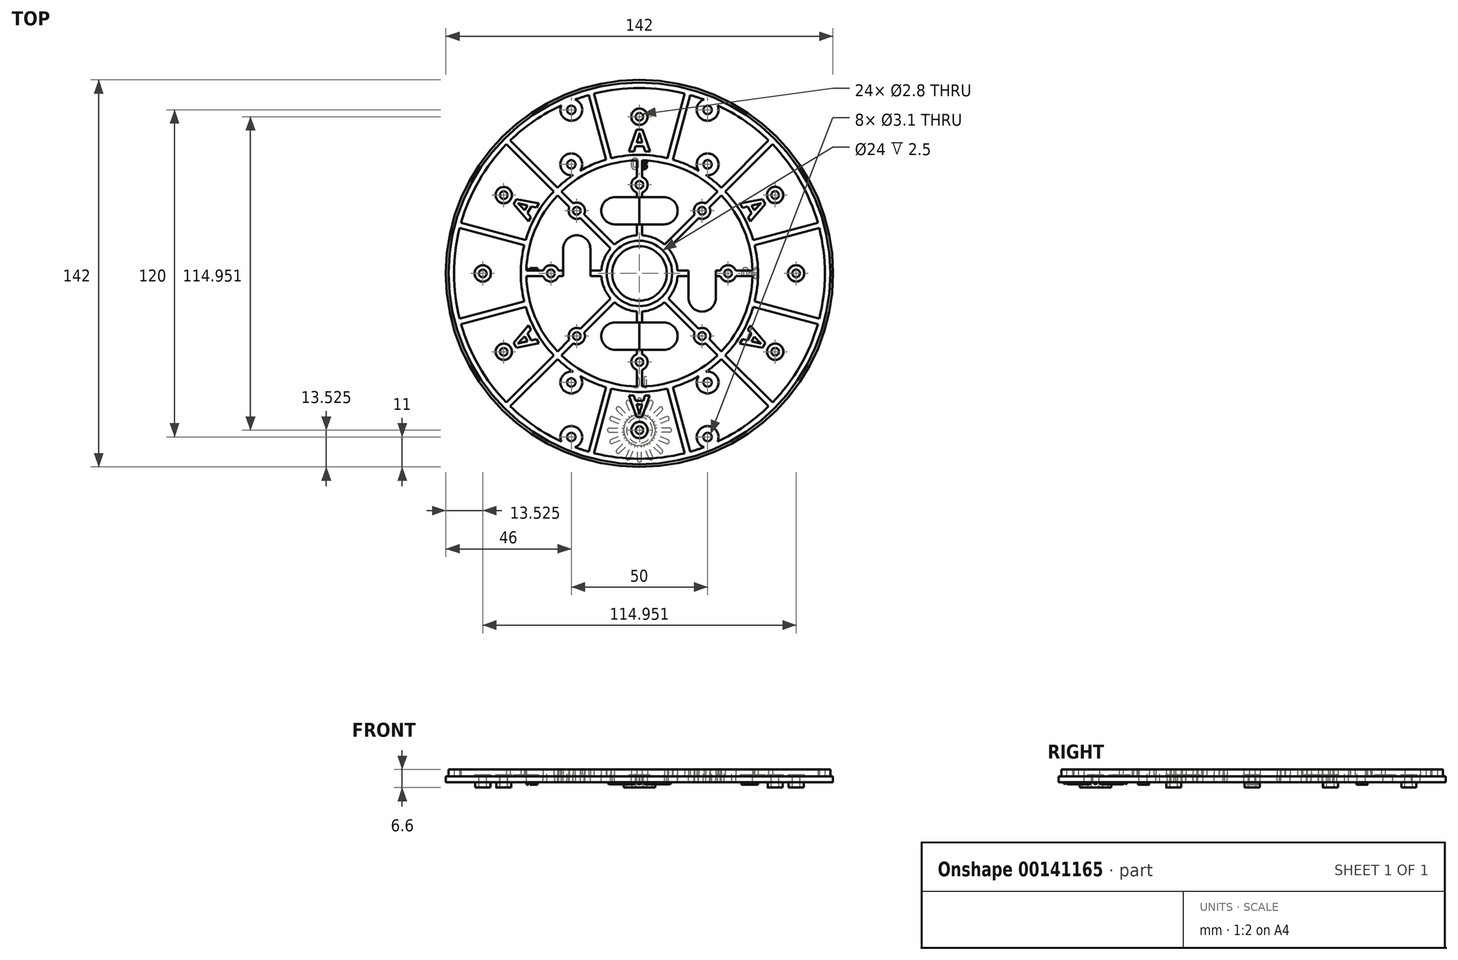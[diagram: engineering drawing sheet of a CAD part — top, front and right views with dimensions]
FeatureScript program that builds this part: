
annotation { "Feature Type Name" : "Feature", "Feature Type Description" : "" }
export const myFeature = defineFeature(function(context is Context, id is Id, definition is map)
    precondition{}
    {
        {
            var Q0;
            Q0=qCreatedBy(makeId("Top.planeOp"),FACE);
            var sketch = newSketch(context, id + "F0", { "sketchPlane" : qUnion([Q0])});
            skCircle(sketch, "E0", {"center": v(0, 0) * mm, "radius": 71 * mm});
            skCircle(sketch, "E1", {"center": v(0, 0) * mm, "radius": 10 * mm});
            skLineSegment(sketch, "E2.top", {"start": v(9, 18) * mm, "end": v(-9, 18) * mm});
            skLineSegment(sketch, "E3.top", {"start": v(-9, 28) * mm, "end": v(9, 28) * mm});
            skCircle(sketch, "E4", {"center": v(0, 0) * mm, "radius": 32.5 * mm, "construction": true});
            skArc(sketch, "E5", {"start": v(-9, 28) * mm, "mid": v(-14, 23) * mm, "end": v(-9, 18) * mm});
            skArc(sketch, "E6.MirrorC", {"start": v(9, 28) * mm, "mid": v(14, 23) * mm, "end": v(9, 18) * mm});
            skLineSegment(sketch, "E7.1.0", {"start": v(-18, 9) * mm, "end": v(-18, -9) * mm});
            skLineSegment(sketch, "E7.1.1", {"start": v(-28, -9) * mm, "end": v(-28, 9) * mm});
            skArc(sketch, "E7.1.2", {"start": v(-28, 9) * mm, "mid": v(-23, 14) * mm, "end": v(-18, 9) * mm});
            skArc(sketch, "E7.1.3", {"start": v(-28, -9) * mm, "mid": v(-23, -14) * mm, "end": v(-18, -9) * mm});
            skLineSegment(sketch, "E7.2.0", {"start": v(-9, -18) * mm, "end": v(9, -18) * mm});
            skLineSegment(sketch, "E7.2.1", {"start": v(9, -28) * mm, "end": v(-9, -28) * mm});
            skArc(sketch, "E7.2.2", {"start": v(-9, -28) * mm, "mid": v(-14, -23) * mm, "end": v(-9, -18) * mm});
            skArc(sketch, "E7.2.3", {"start": v(9, -28) * mm, "mid": v(14, -23) * mm, "end": v(9, -18) * mm});
            skLineSegment(sketch, "E7.3.0", {"start": v(18, -9) * mm, "end": v(18, 9) * mm});
            skLineSegment(sketch, "E7.3.1", {"start": v(28, 9) * mm, "end": v(28, -9) * mm});
            skArc(sketch, "E7.3.2", {"start": v(28, -9) * mm, "mid": v(23, -14) * mm, "end": v(18, -9) * mm});
            skArc(sketch, "E7.3.3", {"start": v(28, 9) * mm, "mid": v(23, 14) * mm, "end": v(18, 9) * mm});
            skCircle(sketch, "E8", {"center": v(0, 0) * mm, "radius": 42.5 * mm, "construction": true});
            skPoint(sketch, "E9", {"position": v(0, 32.5) * mm});
            skCircle(sketch, "E10", {"center": v(0, 0) * mm, "radius": 57.5 * mm, "construction": true});
            skLineSegment(sketch, "E11", {"start": v(-42.5, 0) * mm, "end": v(42.5, 0) * mm, "construction": true});
            skLineSegment(sketch, "E12", {"start": v(0, 42.5) * mm, "end": v(0, -42.5) * mm});
            skLineSegment(sketch, "E13", {"start": v(-7.07, 7.07) * mm, "end": v(-50.2, 50.2) * mm, "construction": true});
            skArc(sketch, "E14.0", {"start": v(-48.79, 47.37) * mm, "mid": v(-58.89, 34) * mm, "end": v(-65.42, 18.56) * mm});
            skCircle(sketch, "E15.0", {"center": v(0, 0) * mm, "radius": 70 * mm});
            skArc(sketch, "E16.0", {"start": v(-31.46, 30.04) * mm, "mid": v(-37.67, 21.75) * mm, "end": v(-41.75, 12.22) * mm});
            skArc(sketch, "E17.0", {"start": v(-41.49, -1) * mm, "mid": v(-38.34, -15.88) * mm, "end": v(-30.04, -28.63) * mm});
            skCircle(sketch, "E18.0", {"center": v(0, 0) * mm, "radius": 12 * mm});
            skArc(sketch, "E19.0", {"start": v(-10.58, 9.17) * mm, "mid": v(-12.93, 5.36) * mm, "end": v(-13.96, 1) * mm});
            skLineSegment(sketch, "E20.0", {"start": v(1, 42.5) * mm, "end": v(1, 42.49) * mm});
            skLineSegment(sketch, "E21.0", {"start": v(-1, 42.5) * mm, "end": v(-1, 42.49) * mm});
            skLineSegment(sketch, "E22.0", {"start": v(-42.5, -1) * mm, "end": v(-42.49, -1) * mm});
            skLineSegment(sketch, "E23.0", {"start": v(-42.5, 1) * mm, "end": v(-42.49, 1) * mm});
            skLineSegment(sketch, "E24.trimOffspring", {"start": v(-9.17, 10.58) * mm, "end": v(-20.27, 21.69) * mm});
            skLineSegment(sketch, "E25.trimOffspring", {"start": v(-10.58, 9.17) * mm, "end": v(-21.69, 20.27) * mm});
            skLineSegment(sketch, "E26.trimOffspring", {"start": v(13.96, -1) * mm, "end": v(18, -1) * mm});
            skLineSegment(sketch, "E27.trimOffspring", {"start": v(13.96, 1) * mm, "end": v(18, 1) * mm});
            skLineSegment(sketch, "E28.trimOffspring", {"start": v(-1, -13.96) * mm, "end": v(-1, -18) * mm});
            skLineSegment(sketch, "E29.trimOffspring", {"start": v(1, -13.96) * mm, "end": v(1, -18) * mm});
            skArc(sketch, "E30.trimOffspring", {"start": v(-1, 13.96) * mm, "mid": v(-5.36, 12.93) * mm, "end": v(-9.17, 10.58) * mm});
            skArc(sketch, "E31.trimOffspring", {"start": v(13.96, 1) * mm, "mid": v(12.93, 5.36) * mm, "end": v(10.58, 9.17) * mm});
            skArc(sketch, "E32.trimOffspring", {"start": v(1, -13.96) * mm, "mid": v(9.9, -9.9) * mm, "end": v(13.96, -1) * mm});
            skArc(sketch, "E33.trimOffspring", {"start": v(-13.96, -1) * mm, "mid": v(-9.9, -9.9) * mm, "end": v(-1, -13.96) * mm});
            skLineSegment(sketch, "E34.trimOffspring", {"start": v(-41.49, 1) * mm, "end": v(-35.33, 1) * mm});
            skLineSegment(sketch, "E35.trimOffspring", {"start": v(-41.49, -1) * mm, "end": v(-35.33, -1) * mm});
            skArc(sketch, "E36.trimOffspring", {"start": v(-1, 41.49) * mm, "mid": v(-15.88, 38.34) * mm, "end": v(-28.63, 30.04) * mm});
            skLineSegment(sketch, "E37.trimOffspring", {"start": v(-1, 41.49) * mm, "end": v(-1, 35.33) * mm});
            skLineSegment(sketch, "E38.trimOffspring", {"start": v(1, 41.49) * mm, "end": v(1, 35.33) * mm});
            skLineSegment(sketch, "E39.trimOffspring", {"start": v(-30.04, 31.46) * mm, "end": v(-47.37, 48.79) * mm});
            skArc(sketch, "E40.trimOffspring", {"start": v(-30.04, 28.63) * mm, "mid": v(-38.34, 15.88) * mm, "end": v(-41.49, 1) * mm});
            skLineSegment(sketch, "E41.trimOffspring", {"start": v(-31.46, 30.04) * mm, "end": v(-48.79, 47.37) * mm});
            skLineSegment(sketch, "E42.1.0", {"start": v(-9.17, -10.58) * mm, "end": v(-20.27, -21.69) * mm});
            skLineSegment(sketch, "E42.1.1", {"start": v(-10.58, -9.17) * mm, "end": v(-21.69, -20.27) * mm});
            skLineSegment(sketch, "E42.1.2", {"start": v(-7.07, -7.07) * mm, "end": v(-50.2, -50.2) * mm, "construction": true});
            skLineSegment(sketch, "E42.2.0", {"start": v(10.58, -9.17) * mm, "end": v(21.69, -20.27) * mm});
            skLineSegment(sketch, "E42.2.1", {"start": v(9.17, -10.58) * mm, "end": v(20.27, -21.69) * mm});
            skLineSegment(sketch, "E42.2.2", {"start": v(7.07, -7.07) * mm, "end": v(50.2, -50.2) * mm, "construction": true});
            skLineSegment(sketch, "E42.3.0", {"start": v(9.17, 10.58) * mm, "end": v(20.27, 21.69) * mm});
            skLineSegment(sketch, "E42.3.1", {"start": v(10.58, 9.17) * mm, "end": v(21.69, 20.27) * mm});
            skLineSegment(sketch, "E42.3.2", {"start": v(7.07, 7.07) * mm, "end": v(50.2, 50.2) * mm, "construction": true});
            skLineSegment(sketch, "E43.1.0", {"start": v(-41.75, 12.22) * mm, "end": v(-65.42, 18.56) * mm});
            skLineSegment(sketch, "E43.1.1", {"start": v(-42.27, 10.29) * mm, "end": v(-65.93, 16.63) * mm});
            skLineSegment(sketch, "E43.2.0", {"start": v(-42.27, -10.29) * mm, "end": v(-65.93, -16.63) * mm});
            skLineSegment(sketch, "E43.2.1", {"start": v(-41.75, -12.22) * mm, "end": v(-65.42, -18.56) * mm});
            skLineSegment(sketch, "E43.3.0", {"start": v(-31.46, -30.04) * mm, "end": v(-48.79, -47.37) * mm});
            skLineSegment(sketch, "E43.3.1", {"start": v(-30.04, -31.46) * mm, "end": v(-47.37, -48.79) * mm});
            skLineSegment(sketch, "E43.4.0", {"start": v(-12.22, -41.75) * mm, "end": v(-18.56, -65.42) * mm});
            skLineSegment(sketch, "E43.4.1", {"start": v(-10.29, -42.27) * mm, "end": v(-16.63, -65.93) * mm});
            skLineSegment(sketch, "E43.5.0", {"start": v(10.29, -42.27) * mm, "end": v(16.63, -65.93) * mm});
            skLineSegment(sketch, "E43.5.1", {"start": v(12.22, -41.75) * mm, "end": v(18.56, -65.42) * mm});
            skLineSegment(sketch, "E43.6.0", {"start": v(30.04, -31.46) * mm, "end": v(47.37, -48.79) * mm});
            skLineSegment(sketch, "E43.6.1", {"start": v(31.46, -30.04) * mm, "end": v(48.79, -47.37) * mm});
            skLineSegment(sketch, "E43.7.0", {"start": v(41.75, -12.22) * mm, "end": v(65.42, -18.56) * mm});
            skLineSegment(sketch, "E43.7.1", {"start": v(42.27, -10.29) * mm, "end": v(65.93, -16.63) * mm});
            skLineSegment(sketch, "E43.8.0", {"start": v(42.27, 10.29) * mm, "end": v(65.93, 16.63) * mm});
            skLineSegment(sketch, "E43.8.1", {"start": v(41.75, 12.22) * mm, "end": v(65.42, 18.56) * mm});
            skLineSegment(sketch, "E43.9.0", {"start": v(31.46, 30.04) * mm, "end": v(48.79, 47.37) * mm});
            skLineSegment(sketch, "E43.9.1", {"start": v(30.04, 31.46) * mm, "end": v(47.37, 48.79) * mm});
            skLineSegment(sketch, "E43.10.0", {"start": v(12.22, 41.75) * mm, "end": v(18.56, 65.42) * mm});
            skLineSegment(sketch, "E43.10.1", {"start": v(10.29, 42.27) * mm, "end": v(16.63, 65.93) * mm});
            skLineSegment(sketch, "E43.11.0", {"start": v(-10.29, 42.27) * mm, "end": v(-16.63, 65.93) * mm});
            skLineSegment(sketch, "E43.11.1", {"start": v(-12.22, 41.75) * mm, "end": v(-18.56, 65.42) * mm});
            skArc(sketch, "E44.trimOffspring", {"start": v(-65.93, 16.63) * mm, "mid": v(-68, 0) * mm, "end": v(-65.93, -16.63) * mm});
            skArc(sketch, "E45.trimOffspring", {"start": v(-65.42, -18.56) * mm, "mid": v(-58.89, -34) * mm, "end": v(-48.79, -47.37) * mm});
            skArc(sketch, "E46.trimOffspring", {"start": v(-47.37, -48.79) * mm, "mid": v(-38.54, -56.02) * mm, "end": v(-28.63, -61.68) * mm});
            skArc(sketch, "E47.trimOffspring", {"start": v(-16.63, -65.93) * mm, "mid": v(0, -68) * mm, "end": v(16.63, -65.93) * mm});
            skArc(sketch, "E48.trimOffspring", {"start": v(18.56, -65.42) * mm, "mid": v(21.12, -64.64) * mm, "end": v(23.64, -63.76) * mm});
            skArc(sketch, "E49.trimOffspring", {"start": v(12.22, -41.75) * mm, "mid": v(17.1, -40) * mm, "end": v(21.75, -37.67) * mm});
            skArc(sketch, "E50.trimOffspring", {"start": v(48.79, -47.37) * mm, "mid": v(58.89, -34) * mm, "end": v(65.42, -18.56) * mm});
            skArc(sketch, "E51.trimOffspring", {"start": v(31.46, -30.04) * mm, "mid": v(37.67, -21.75) * mm, "end": v(41.75, -12.22) * mm});
            skArc(sketch, "E52.trimOffspring", {"start": v(30.04, -28.63) * mm, "mid": v(38.34, -15.88) * mm, "end": v(41.49, -1) * mm});
            skLineSegment(sketch, "E53.trimOffspring", {"start": v(-1, -42.49) * mm, "end": v(-1, -42.5) * mm});
            skLineSegment(sketch, "E54.trimOffspring", {"start": v(1, -42.49) * mm, "end": v(1, -42.5) * mm});
            skArc(sketch, "E55.trimOffspring", {"start": v(1, -41.49) * mm, "mid": v(15.88, -38.34) * mm, "end": v(28.63, -30.04) * mm});
            skArc(sketch, "E56.trimOffspring", {"start": v(65.93, -16.63) * mm, "mid": v(65.68, 17.6) * mm, "end": v(48.79, 47.37) * mm});
            skArc(sketch, "E57.trimOffspring", {"start": v(42.27, -10.29) * mm, "mid": v(43.5, 0) * mm, "end": v(42.27, 10.29) * mm});
            skArc(sketch, "E58.trimOffspring", {"start": v(41.75, 12.22) * mm, "mid": v(37.67, 21.75) * mm, "end": v(31.46, 30.04) * mm});
            skLineSegment(sketch, "E59.trimOffspring", {"start": v(28, 1) * mm, "end": v(29.67, 1) * mm});
            skLineSegment(sketch, "E60.trimOffspring", {"start": v(28, -1) * mm, "end": v(29.67, -1) * mm});
            skLineSegment(sketch, "E61.trimOffspring", {"start": v(42.49, 1) * mm, "end": v(42.5, 1) * mm});
            skLineSegment(sketch, "E62.trimOffspring", {"start": v(42.49, -1) * mm, "end": v(42.5, -1) * mm});
            skArc(sketch, "E63.trimOffspring", {"start": v(41.49, 1) * mm, "mid": v(38.34, 15.88) * mm, "end": v(30.04, 28.63) * mm});
            skArc(sketch, "E64.trimOffspring", {"start": v(47.37, 48.79) * mm, "mid": v(38.54, 56.02) * mm, "end": v(28.63, 61.68) * mm});
            skArc(sketch, "E65.trimOffspring", {"start": v(30.04, 31.46) * mm, "mid": v(27.29, 33.88) * mm, "end": v(24.34, 36.06) * mm});
            skArc(sketch, "E66.trimOffspring", {"start": v(28.63, 30.04) * mm, "mid": v(15.88, 38.34) * mm, "end": v(1, 41.49) * mm});
            skArc(sketch, "E67.trimOffspring", {"start": v(10.29, 42.27) * mm, "mid": v(0, 43.5) * mm, "end": v(-10.29, 42.27) * mm});
            skArc(sketch, "E68.trimOffspring", {"start": v(16.63, 65.93) * mm, "mid": v(0, 68) * mm, "end": v(-16.63, 65.93) * mm});
            skArc(sketch, "E69.trimOffspring", {"start": v(-12.22, 41.75) * mm, "mid": v(-17.1, 40) * mm, "end": v(-21.75, 37.67) * mm});
            skArc(sketch, "E70.trimOffspring", {"start": v(-18.56, 65.42) * mm, "mid": v(-21.12, 64.64) * mm, "end": v(-23.64, 63.76) * mm});
            skArc(sketch, "E71.trimOffspring", {"start": v(-42.27, 10.29) * mm, "mid": v(-43.5, 0) * mm, "end": v(-42.27, -10.29) * mm});
            skArc(sketch, "E72.trimOffspring", {"start": v(-41.75, -12.22) * mm, "mid": v(-37.67, -21.75) * mm, "end": v(-31.46, -30.04) * mm});
            skLineSegment(sketch, "E73.trimOffspring", {"start": v(-18, -1) * mm, "end": v(-13.96, -1) * mm});
            skLineSegment(sketch, "E74.trimOffspring", {"start": v(-18, 1) * mm, "end": v(-13.96, 1) * mm});
            skArc(sketch, "E75.trimOffspring", {"start": v(-28.63, -30.04) * mm, "mid": v(-15.88, -38.34) * mm, "end": v(-1, -41.49) * mm});
            skArc(sketch, "E76.trimOffspring", {"start": v(-30.04, -31.46) * mm, "mid": v(-27.29, -33.88) * mm, "end": v(-24.34, -36.06) * mm});
            skArc(sketch, "E77.trimOffspring", {"start": v(-10.29, -42.27) * mm, "mid": v(0, -43.5) * mm, "end": v(10.29, -42.27) * mm});
            skLineSegment(sketch, "E78.trimOffspring", {"start": v(-1, -28) * mm, "end": v(-1, -29.67) * mm});
            skLineSegment(sketch, "E79.trimOffspring", {"start": v(1, -28) * mm, "end": v(1, -29.67) * mm});
            skLineSegment(sketch, "E80.trimOffspring", {"start": v(1, 18) * mm, "end": v(1, 13.96) * mm});
            skLineSegment(sketch, "E81.trimOffspring", {"start": v(-1, 18) * mm, "end": v(-1, 13.96) * mm});
            skArc(sketch, "E82.trimOffspring", {"start": v(9.17, 10.58) * mm, "mid": v(5.36, 12.93) * mm, "end": v(1, 13.96) * mm});
            skCircle(sketch, "E83", {"center": v(0, 32.5) * mm, "radius": 1.4 * mm});
            skArc(sketch, "E84", {"start": v(-1, 35.33) * mm, "mid": v(-3, 32.5) * mm, "end": v(-1, 29.67) * mm});
            skArc(sketch, "E85.1.0", {"start": v(-20.27, 21.69) * mm, "mid": v(-20.86, 25.1) * mm, "end": v(-24.27, 25.69) * mm});
            skCircle(sketch, "E85.1.1", {"center": v(-22.98, 22.98) * mm, "radius": 1.4 * mm});
            skArc(sketch, "E85.2.0", {"start": v(-29.67, 1) * mm, "mid": v(-32.5, 3) * mm, "end": v(-35.33, 1) * mm});
            skCircle(sketch, "E85.2.1", {"center": v(-32.5, 0) * mm, "radius": 1.4 * mm});
            skArc(sketch, "E85.3.0", {"start": v(-24.27, -25.69) * mm, "mid": v(-20.86, -25.1) * mm, "end": v(-20.27, -21.69) * mm});
            skCircle(sketch, "E85.3.1", {"center": v(-22.98, -22.98) * mm, "radius": 1.4 * mm});
            skArc(sketch, "E85.4.0", {"start": v(1, -35.33) * mm, "mid": v(3, -32.5) * mm, "end": v(1, -29.67) * mm});
            skCircle(sketch, "E85.4.1", {"center": v(0, -32.5) * mm, "radius": 1.4 * mm});
            skArc(sketch, "E85.5.0", {"start": v(25.69, -24.27) * mm, "mid": v(25.1, -20.86) * mm, "end": v(21.69, -20.27) * mm});
            skCircle(sketch, "E85.5.1", {"center": v(22.98, -22.98) * mm, "radius": 1.4 * mm});
            skArc(sketch, "E85.6.0", {"start": v(35.33, 1) * mm, "mid": v(32.5, 3) * mm, "end": v(29.67, 1) * mm});
            skCircle(sketch, "E85.6.1", {"center": v(32.5, 0) * mm, "radius": 1.4 * mm});
            skArc(sketch, "E85.7.0", {"start": v(24.27, 25.69) * mm, "mid": v(20.86, 25.1) * mm, "end": v(20.27, 21.69) * mm});
            skCircle(sketch, "E85.7.1", {"center": v(22.98, 22.98) * mm, "radius": 1.4 * mm});
            skCircle(sketch, "E86", {"center": v(-0.02, 57.48) * mm, "radius": 1.4 * mm});
            skCircle(sketch, "E87", {"center": v(-0.02, 57.48) * mm, "radius": 3 * mm});
            skCircle(sketch, "E88.2.0", {"center": v(-49.78, 28.72) * mm, "radius": 1.4 * mm});
            skCircle(sketch, "E88.2.1", {"center": v(-49.78, 28.72) * mm, "radius": 3 * mm});
            skCircle(sketch, "E88.3.0", {"center": v(-57.48, -0.02) * mm, "radius": 1.4 * mm});
            skCircle(sketch, "E88.3.1", {"center": v(-57.48, -0.02) * mm, "radius": 3 * mm});
            skCircle(sketch, "E88.4.0", {"center": v(-49.77, -28.75) * mm, "radius": 1.4 * mm});
            skCircle(sketch, "E88.4.1", {"center": v(-49.77, -28.75) * mm, "radius": 3 * mm});
            skCircle(sketch, "E88.6.0", {"center": v(0.02, -57.48) * mm, "radius": 1.4 * mm});
            skCircle(sketch, "E88.6.1", {"center": v(0.02, -57.48) * mm, "radius": 3 * mm});
            skLineSegment(sketch, "E89.trimOffspring", {"start": v(-1, 29.67) * mm, "end": v(-1, 28) * mm});
            skLineSegment(sketch, "E90.trimOffspring", {"start": v(1, 29.67) * mm, "end": v(1, 28) * mm});
            skArc(sketch, "E91.trimOffspring", {"start": v(1, 29.67) * mm, "mid": v(3, 32.5) * mm, "end": v(1, 35.33) * mm});
            skLineSegment(sketch, "E92.trimOffspring", {"start": v(25.69, 24.27) * mm, "end": v(30.04, 28.63) * mm});
            skLineSegment(sketch, "E93.trimOffspring", {"start": v(24.27, 25.69) * mm, "end": v(28.63, 30.04) * mm});
            skArc(sketch, "E94.trimOffspring", {"start": v(21.69, 20.27) * mm, "mid": v(25.1, 20.86) * mm, "end": v(25.69, 24.27) * mm});
            skLineSegment(sketch, "E95.trimOffspring", {"start": v(35.33, -1) * mm, "end": v(41.49, -1) * mm});
            skArc(sketch, "E96.trimOffspring", {"start": v(29.67, -1) * mm, "mid": v(32.5, -3) * mm, "end": v(35.33, -1) * mm});
            skLineSegment(sketch, "E97.trimOffspring", {"start": v(35.33, 1) * mm, "end": v(41.49, 1) * mm});
            skLineSegment(sketch, "E98.trimOffspring", {"start": v(24.27, -25.69) * mm, "end": v(28.63, -30.04) * mm});
            skArc(sketch, "E99.trimOffspring", {"start": v(20.27, -21.69) * mm, "mid": v(20.86, -25.1) * mm, "end": v(24.27, -25.69) * mm});
            skLineSegment(sketch, "E100.trimOffspring", {"start": v(25.69, -24.27) * mm, "end": v(30.04, -28.63) * mm});
            skLineSegment(sketch, "E101.trimOffspring", {"start": v(-1, -35.33) * mm, "end": v(-1, -41.49) * mm});
            skLineSegment(sketch, "E102.trimOffspring", {"start": v(1, -35.33) * mm, "end": v(1, -41.49) * mm});
            skArc(sketch, "E103.trimOffspring", {"start": v(-1, -29.67) * mm, "mid": v(-3, -32.5) * mm, "end": v(-1, -35.33) * mm});
            skLineSegment(sketch, "E104.trimOffspring", {"start": v(-25.69, -24.27) * mm, "end": v(-30.04, -28.63) * mm});
            skArc(sketch, "E105.trimOffspring", {"start": v(-21.69, -20.27) * mm, "mid": v(-25.1, -20.86) * mm, "end": v(-25.69, -24.27) * mm});
            skLineSegment(sketch, "E106.trimOffspring", {"start": v(-24.27, -25.69) * mm, "end": v(-28.63, -30.04) * mm});
            skLineSegment(sketch, "E107.trimOffspring", {"start": v(-29.67, 1) * mm, "end": v(-28, 1) * mm});
            skArc(sketch, "E108.trimOffspring", {"start": v(-35.33, -1) * mm, "mid": v(-32.5, -3) * mm, "end": v(-29.67, -1) * mm});
            skLineSegment(sketch, "E109.trimOffspring", {"start": v(-29.67, -1) * mm, "end": v(-28, -1) * mm});
            skLineSegment(sketch, "E110.trimOffspring", {"start": v(-24.27, 25.69) * mm, "end": v(-28.63, 30.04) * mm});
            skArc(sketch, "E111.trimOffspring", {"start": v(-25.69, 24.27) * mm, "mid": v(-25.1, 20.86) * mm, "end": v(-21.69, 20.27) * mm});
            skLineSegment(sketch, "E112.trimOffspring", {"start": v(-25.69, 24.27) * mm, "end": v(-30.04, 28.63) * mm});
            skCircle(sketch, "E113", {"center": v(-25, 40) * mm, "radius": 1.55 * mm});
            skArc(sketch, "E114", {"start": v(-21.75, 37.67) * mm, "mid": v(-27.12, 43.4) * mm, "end": v(-24.34, 36.06) * mm});
            skArc(sketch, "E115.trimOffspring", {"start": v(-24.34, 36.06) * mm, "mid": v(-27.29, 33.88) * mm, "end": v(-30.04, 31.46) * mm});
            skArc(sketch, "E116.trimOffspring", {"start": v(21.75, 37.67) * mm, "mid": v(17.1, 40) * mm, "end": v(12.22, 41.75) * mm});
            skArc(sketch, "E117.trimOffspring", {"start": v(24.34, -36.06) * mm, "mid": v(27.29, -33.88) * mm, "end": v(30.04, -31.46) * mm});
            skArc(sketch, "E118.trimOffspring", {"start": v(-21.75, -37.67) * mm, "mid": v(-17.1, -40) * mm, "end": v(-12.22, -41.75) * mm});
            skText(sketch, "E119", { "text": "A", "fontName": "OpenSans-Bold.ttf"});
            skCircle(sketch, "E120.1.8.0", {"center": v(49.78, -28.72) * mm, "radius": 1.4 * mm});
            skCircle(sketch, "E120.2.8.0", {"center": v(49.78, -28.72) * mm, "radius": 3 * mm});
            skCircle(sketch, "E120.1.9.0", {"center": v(57.48, 0.02) * mm, "radius": 1.4 * mm});
            skCircle(sketch, "E120.2.9.0", {"center": v(57.48, 0.02) * mm, "radius": 3 * mm});
            skCircle(sketch, "E120.1.10.0", {"center": v(49.77, 28.75) * mm, "radius": 1.4 * mm});
            skCircle(sketch, "E120.2.10.0", {"center": v(49.77, 28.75) * mm, "radius": 3 * mm});
            skCircle(sketch, "E121", {"center": v(-25, 60) * mm, "radius": 1.55 * mm});
            skArc(sketch, "E122", {"start": v(-28.63, 61.68) * mm, "mid": v(-23.46, 56.3) * mm, "end": v(-23.64, 63.76) * mm});
            skCircle(sketch, "E123.MirrorC", {"center": v(25, 40) * mm, "radius": 1.55 * mm});
            skArc(sketch, "E124.MirrorCS", {"start": v(21.75, 37.67) * mm, "mid": v(27.12, 43.4) * mm, "end": v(24.34, 36.06) * mm});
            skArc(sketch, "E125.MirrorC", {"start": v(28.63, 61.68) * mm, "mid": v(23.46, 56.3) * mm, "end": v(23.64, 63.76) * mm});
            skCircle(sketch, "E126.MirrorC", {"center": v(25, 60) * mm, "radius": 1.55 * mm});
            skArc(sketch, "E127.MirrorCS", {"start": v(21.75, -37.67) * mm, "mid": v(27.12, -43.4) * mm, "end": v(24.34, -36.06) * mm});
            skCircle(sketch, "E128.MirrorC", {"center": v(25, -40) * mm, "radius": 1.55 * mm});
            skArc(sketch, "E129.MirrorC", {"start": v(28.63, -61.68) * mm, "mid": v(23.46, -56.3) * mm, "end": v(23.64, -63.76) * mm});
            skCircle(sketch, "E130.MirrorC", {"center": v(25, -60) * mm, "radius": 1.55 * mm});
            skArc(sketch, "E131.MirrorC", {"start": v(-28.63, -61.68) * mm, "mid": v(-23.46, -56.3) * mm, "end": v(-23.64, -63.76) * mm});
            skCircle(sketch, "E132.MirrorC", {"center": v(-25, -60) * mm, "radius": 1.55 * mm});
            skArc(sketch, "E133.MirrorCS", {"start": v(-21.75, -37.67) * mm, "mid": v(-27.12, -43.4) * mm, "end": v(-24.34, -36.06) * mm});
            skCircle(sketch, "E134.MirrorC", {"center": v(-25, -40) * mm, "radius": 1.55 * mm});
            skArc(sketch, "E135.trimOffspring", {"start": v(-28.63, 61.68) * mm, "mid": v(-38.54, 56.02) * mm, "end": v(-47.37, 48.79) * mm});
            skArc(sketch, "E136.trimOffspring", {"start": v(23.64, 63.76) * mm, "mid": v(21.12, 64.64) * mm, "end": v(18.56, 65.42) * mm});
            skArc(sketch, "E137.trimOffspring", {"start": v(28.63, -61.68) * mm, "mid": v(38.54, -56.02) * mm, "end": v(47.37, -48.79) * mm});
            skArc(sketch, "E138.trimOffspring", {"start": v(-23.64, -63.76) * mm, "mid": v(-21.12, -64.64) * mm, "end": v(-18.56, -65.42) * mm});
            const initialGuessF0  = {"E119": [-0.00381, 0.04475, 1, 0, 0.008]};
            skSetInitialGuess(sketch, initialGuessF0);
            skSolve(sketch);
        }
        {
            var Q0;
            Q0=makeQuery(id+"F0.imprint","IMPRINT",FACE,{"disambiguationData":[TD([[makeQuery(id+"F0.imprint","IMPRINT",EDGE,{"derivedFrom":sQuery(id+"F0.wireOp",EDGE,"E39.trimOffspring")}),-1.0]])]});
            var Q1;
            Q1=makeQuery(id+"F0.imprint","IMPRINT",FACE,{"disambiguationData":[TD([[makeQuery(id+"F0.imprint","IMPRINT",EDGE,{"derivedFrom":sQuery(id+"F0.wireOp",EDGE,"E43.5.1")}),1.0]])]});
            var Q2;
            {var subQ0=sQuery(id+"F0.wireOp",EDGE,"E5");Q2=makeQuery(id+"F0.imprint","IMPRINT",FACE,{"disambiguationData":[TD([[makeQuery(id+"F0.imprint","IMPRINT",EDGE,{"derivedFrom":subQ0}),-1.0]])]});}
            var Q3;
            Q3=makeQuery(id+"F0.imprint","IMPRINT",FACE,{"disambiguationData":[TD([[makeQuery(id+"F0.imprint","IMPRINT",EDGE,{"derivedFrom":sQuery(id+"F0.wireOp",EDGE,"E43.9.1")}),1.0]])]});
            var Q4;
            Q4=makeQuery(id+"F0.imprint","IMPRINT",FACE,{"disambiguationData":[TD([[makeQuery(id+"F0.imprint","IMPRINT",EDGE,{"derivedFrom":sQuery(id+"F0.wireOp",EDGE,"E43.2.1")}),1.0]])]});
            var Q5;
            {var subQ0=sQuery(id+"F0.wireOp",EDGE,"E43.7.1");Q5=makeQuery(id+"F0.imprint","IMPRINT",FACE,{"disambiguationData":[TD([[makeQuery(id+"F0.imprint","IMPRINT",EDGE,{"derivedFrom":subQ0}),1.0]])]});}
            var Q6;
            {var subQ3=sQuery(id+"F0.wireOp",EDGE,"E7.2.2");Q6=makeQuery(id+"F0.imprint","IMPRINT",FACE,{"disambiguationData":[TD([[makeQuery(id+"F0.imprint","IMPRINT",EDGE,{"derivedFrom":subQ3}),1.0]])]});}
            var Q7;
            {var subQ0=sQuery(id+"F0.wireOp",EDGE,"E43.8.1");Q7=makeQuery(id+"F0.imprint","IMPRINT",FACE,{"disambiguationData":[TD([[makeQuery(id+"F0.imprint","IMPRINT",EDGE,{"derivedFrom":subQ0}),1.0]])]});}
            var Q8;
            {var subQ0=sQuery(id+"F0.wireOp",EDGE,"E7.3.2");Q8=makeQuery(id+"F0.imprint","IMPRINT",FACE,{"disambiguationData":[TD([[makeQuery(id+"F0.imprint","IMPRINT",EDGE,{"derivedFrom":subQ0}),1.0]])]});}
            var Q9;
            {var subQ0=sQuery(id+"F0.wireOp",EDGE,"E7.1.3");Q9=makeQuery(id+"F0.imprint","IMPRINT",FACE,{"disambiguationData":[TD([[makeQuery(id+"F0.imprint","IMPRINT",EDGE,{"derivedFrom":subQ0}),-1.0]])]});}
            var Q10;
            Q10=makeQuery(id+"F0.imprint","IMPRINT",FACE,{"disambiguationData":[TD([[makeQuery(id+"F0.imprint","IMPRINT",EDGE,{"derivedFrom":sQuery(id+"F0.wireOp",EDGE,"E43.4.1")}),1.0]])]});
            var Q11;
            Q11=makeQuery(id+"F0.imprint","IMPRINT",FACE,{"disambiguationData":[TD([[makeQuery(id+"F0.imprint","IMPRINT",EDGE,{"derivedFrom":sQuery(id+"F0.wireOp",EDGE,"E43.6.1")}),1.0]])]});
            var Q12;
            Q12=makeQuery(id+"F0.imprint","IMPRINT",FACE,{"disambiguationData":[TD([[makeQuery(id+"F0.imprint","IMPRINT",EDGE,{"derivedFrom":sQuery(id+"F0.wireOp",EDGE,"E43.10.1")}),1.0]])]});
            var Q13;
            Q13=makeQuery(id+"F0.imprint","IMPRINT",FACE,{"disambiguationData":[TD([[makeQuery(id+"F0.imprint","IMPRINT",EDGE,{"derivedFrom":sQuery(id+"F0.wireOp",EDGE,"E43.3.1")}),1.0]])]});
            var Q14;
            Q14=makeQuery(id+"F0.imprint","IMPRINT",FACE,{"disambiguationData":[TD([[makeQuery(id+"F0.imprint","IMPRINT",EDGE,{"derivedFrom":sQuery(id+"F0.wireOp",EDGE,"E43.1.1")}),1.0]])]});
            var Q15;
            Q15=makeQuery(id+"F0.imprint","IMPRINT",FACE,{"disambiguationData":[TD([[makeQuery(id+"F0.imprint","IMPRINT",EDGE,{"derivedFrom":sQuery(id+"F0.wireOp",EDGE,"E14.0")}),1.0]])]});
            var Q16;
            Q16=makeQuery(id+"F0.imprint","IMPRINT",FACE,{"disambiguationData":[TD([[makeQuery(id+"F0.imprint","IMPRINT",EDGE,{"derivedFrom":sQuery(id+"F0.wireOp",EDGE,"E15.0")}),-1.0]])]});
            var Q17;
            {var subQ1=sQuery(id+"F0.wireOp",EDGE,"E7.2.3");Q17=makeQuery(id+"F0.imprint","IMPRINT",FACE,{"disambiguationData":[TD([[makeQuery(id+"F0.imprint","IMPRINT",EDGE,{"derivedFrom":subQ1}),-1.0]])]});}
            var Q18;
            {var subQ1=sQuery(id+"F0.wireOp",EDGE,"E6.MirrorC");Q18=makeQuery(id+"F0.imprint","IMPRINT",FACE,{"disambiguationData":[TD([[makeQuery(id+"F0.imprint","IMPRINT",EDGE,{"derivedFrom":subQ1}),1.0]])]});}
            var Q19;
            {var subQ0=sQuery(id+"F0.wireOp",EDGE,"E12");var subQ1=sQuery(id+"F0.wireOp",EDGE,"E1");var subQ2=makeQuery(id+"F0.imprint","INTERSECT",VERTEX,{"disambiguationData":[OD(0.0)],"derivedFrom":[subQ1,subQ0]});Q19=makeQuery(id+"F0.imprint","IMPRINT",FACE,{"disambiguationData":[TD([[makeQuery(id+"F0.imprint","IMPRINT",EDGE,{"disambiguationData":[TD([[subQ2,-1.0]])],"derivedFrom":subQ1}),-1.0]])]});}
            var Q20;
            {var subQ0=sQuery(id+"F0.wireOp",EDGE,"E7.1.2");Q20=makeQuery(id+"F0.imprint","IMPRINT",FACE,{"disambiguationData":[TD([[makeQuery(id+"F0.imprint","IMPRINT",EDGE,{"derivedFrom":subQ0}),1.0]])]});}
            var Q21;
            {var subQ1=sQuery(id+"F0.wireOp",EDGE,"E7.3.3");Q21=makeQuery(id+"F0.imprint","IMPRINT",FACE,{"disambiguationData":[TD([[makeQuery(id+"F0.imprint","IMPRINT",EDGE,{"derivedFrom":subQ1}),-1.0]])]});}
            var Q22;
            {var subQ0=sQuery(id+"F0.wireOp",EDGE,"E12");var subQ1=sQuery(id+"F0.wireOp",EDGE,"E1");var subQ2=makeQuery(id+"F0.imprint","INTERSECT",VERTEX,{"disambiguationData":[OD(0.0)],"derivedFrom":[subQ1,subQ0]});Q22=makeQuery(id+"F0.imprint","IMPRINT",FACE,{"disambiguationData":[TD([[makeQuery(id+"F0.imprint","IMPRINT",EDGE,{"disambiguationData":[TD([[subQ2,1.0]])],"derivedFrom":subQ1}),-1.0]])]});}
            var Q23;
            Q23=makeQuery(id+"F0.imprint","IMPRINT",FACE,{"disambiguationData":[TD([[makeQuery(id+"F0.imprint","IMPRINT",EDGE,{"derivedFrom":sQuery(id+"F0.wireOp",EDGE,"E14.0")}),-1.0]])]});
            var Q24;
            Q24=makeQuery(id+"F0.imprint","IMPRINT",FACE,{"disambiguationData":[TD([[makeQuery(id+"F0.imprint","IMPRINT",EDGE,{"derivedFrom":sQuery(id+"F0.wireOp",EDGE,"E86")}),-1.0]])]});
            var Q25;
            Q25=makeQuery(id+"F0.imprint","IMPRINT",FACE,{"disambiguationData":[TD([[makeQuery(id+"F0.imprint","IMPRINT",EDGE,{"derivedFrom":sQuery(id+"F0.wireOp",EDGE,"E88.2.0")}),-1.0]])]});
            var Q26;
            Q26=makeQuery(id+"F0.imprint","IMPRINT",FACE,{"disambiguationData":[TD([[makeQuery(id+"F0.imprint","IMPRINT",EDGE,{"derivedFrom":sQuery(id+"F0.wireOp",EDGE,"E88.10.0")}),-1.0]])]});
            var Q27;
            Q27=makeQuery(id+"F0.imprint","IMPRINT",FACE,{"disambiguationData":[TD([[makeQuery(id+"F0.imprint","IMPRINT",EDGE,{"derivedFrom":sQuery(id+"F0.wireOp",EDGE,"E88.9.0")}),-1.0]])]});
            var Q28;
            Q28=makeQuery(id+"F0.imprint","IMPRINT",FACE,{"disambiguationData":[TD([[makeQuery(id+"F0.imprint","IMPRINT",EDGE,{"derivedFrom":sQuery(id+"F0.wireOp",EDGE,"E88.8.0")}),-1.0]])]});
            var Q29;
            Q29=makeQuery(id+"F0.imprint","IMPRINT",FACE,{"disambiguationData":[TD([[makeQuery(id+"F0.imprint","IMPRINT",EDGE,{"derivedFrom":sQuery(id+"F0.wireOp",EDGE,"E88.6.0")}),-1.0]])]});
            var Q30;
            Q30=makeQuery(id+"F0.imprint","IMPRINT",FACE,{"disambiguationData":[TD([[makeQuery(id+"F0.imprint","IMPRINT",EDGE,{"derivedFrom":sQuery(id+"F0.wireOp",EDGE,"E88.4.0")}),-1.0]])]});
            var Q31;
            Q31=makeQuery(id+"F0.imprint","IMPRINT",FACE,{"disambiguationData":[TD([[makeQuery(id+"F0.imprint","IMPRINT",EDGE,{"derivedFrom":sQuery(id+"F0.wireOp",EDGE,"E88.3.0")}),-1.0]])]});
            var Q32;
            Q32=makeQuery(id+"F0.imprint","IMPRINT",FACE,{"disambiguationData":[TD([[makeQuery(id+"F0.imprint","IMPRINT",EDGE,{"derivedFrom":sQuery(id+"F0.wireOp",EDGE,"E43.4.0")}),-1.0]])]});
            var Q33;
            Q33=makeQuery(id+"F0.imprint","IMPRINT",FACE,{"disambiguationData":[TD([[makeQuery(id+"F0.imprint","IMPRINT",EDGE,{"derivedFrom":sQuery(id+"F0.wireOp",EDGE,"E120.1.10.0")}),-1.0]])]});
            var Q34;
            Q34=makeQuery(id+"F0.imprint","IMPRINT",FACE,{"disambiguationData":[TD([[makeQuery(id+"F0.imprint","IMPRINT",EDGE,{"derivedFrom":sQuery(id+"F0.wireOp",EDGE,"E120.1.9.0")}),-1.0]])]});
            var Q35;
            Q35=makeQuery(id+"F0.imprint","IMPRINT",FACE,{"disambiguationData":[TD([[makeQuery(id+"F0.imprint","IMPRINT",EDGE,{"derivedFrom":sQuery(id+"F0.wireOp",EDGE,"E119.sketch_text.stroke-0")}),-1.0]])]});
            var Q36;
            Q36=makeQuery(id+"F0.imprint","IMPRINT",FACE,{"disambiguationData":[TD([[makeQuery(id+"F0.imprint","IMPRINT",EDGE,{"derivedFrom":sQuery(id+"F0.wireOp",EDGE,"E120.1.8.0")}),-1.0]])]});
            extrude(context, id + "F1", {"entities" : qUnion([Q0, Q1, Q2, Q3, Q4, Q5, Q6, Q7, Q8, Q9, Q10, Q11, Q12, Q13, Q14, Q15, Q16, Q17, Q18, Q19, Q20, Q21, Q22, Q23, Q24, Q25, Q26, Q27, Q28, Q29, Q30, Q31, Q32, Q33, Q34, Q35, Q36]), "oppositeDirection" : true, "depth" : 2.1 * mm});
        }
        {
            var Q0;
            Q0=makeQuery(id+"F0.imprint","IMPRINT",FACE,{"disambiguationData":[TD([[makeQuery(id+"F0.imprint","IMPRINT",EDGE,{"derivedFrom":sQuery(id+"F0.wireOp",EDGE,"E14.0")}),-1.0]])]});
            extrude(context, id + "F2", {"entities" : qUnion([Q0]), "operationType" : NewBodyOperationType.ADD, "depth" : 2.5 * mm});
        }
        {
            var Q0;
            Q0=makeQuery(id+"F0.imprint","IMPRINT",FACE,{"disambiguationData":[TD([[makeQuery(id+"F0.imprint","IMPRINT",EDGE,{"derivedFrom":sQuery(id+"F0.wireOp",EDGE,"E88.6.0")}),-1.0]])]});
            var Q1;
            Q1=makeQuery(id+"F0.imprint","IMPRINT",FACE,{"disambiguationData":[TD([[makeQuery(id+"F0.imprint","IMPRINT",EDGE,{"derivedFrom":sQuery(id+"F0.wireOp",EDGE,"E88.4.0")}),-1.0]])]});
            var Q2;
            Q2=makeQuery(id+"F0.imprint","IMPRINT",FACE,{"disambiguationData":[TD([[makeQuery(id+"F0.imprint","IMPRINT",EDGE,{"derivedFrom":sQuery(id+"F0.wireOp",EDGE,"E88.3.0")}),-1.0]])]});
            var Q3;
            Q3=makeQuery(id+"F0.imprint","IMPRINT",FACE,{"disambiguationData":[TD([[makeQuery(id+"F0.imprint","IMPRINT",EDGE,{"derivedFrom":sQuery(id+"F0.wireOp",EDGE,"E88.2.0")}),-1.0]])]});
            var Q4;
            Q4=makeQuery(id+"F0.imprint","IMPRINT",FACE,{"disambiguationData":[TD([[makeQuery(id+"F0.imprint","IMPRINT",EDGE,{"derivedFrom":sQuery(id+"F0.wireOp",EDGE,"E86")}),-1.0]])]});
            var Q5;
            Q5=makeQuery(id+"F0.imprint","IMPRINT",FACE,{"disambiguationData":[TD([[makeQuery(id+"F0.imprint","IMPRINT",EDGE,{"derivedFrom":sQuery(id+"F0.wireOp",EDGE,"E120.1.8.0")}),-1.0]])]});
            var Q6;
            Q6=makeQuery(id+"F0.imprint","IMPRINT",FACE,{"disambiguationData":[TD([[makeQuery(id+"F0.imprint","IMPRINT",EDGE,{"derivedFrom":sQuery(id+"F0.wireOp",EDGE,"E120.1.9.0")}),-1.0]])]});
            var Q7;
            Q7=makeQuery(id+"F0.imprint","IMPRINT",FACE,{"disambiguationData":[TD([[makeQuery(id+"F0.imprint","IMPRINT",EDGE,{"derivedFrom":sQuery(id+"F0.wireOp",EDGE,"E120.1.10.0")}),-1.0]])]});
            extrude(context, id + "F3", {"entities" : qUnion([Q0, Q1, Q2, Q3, Q4, Q5, Q6, Q7]), "operationType" : NewBodyOperationType.ADD, "depth" : .5 * mm});
        }
        {
            var Q0;
            Q0=makeQuery(id+"F1.opExtrude","CAP_FACE",FACE,{"disambiguationData":[OSD([sQuery(id+"F0.wireOp",EDGE,"E0"),sQuery(id+"F0.wireOp",EDGE,"E1"),sQuery(id+"F0.wireOp",EDGE,"E2.top"),sQuery(id+"F0.wireOp",EDGE,"E3.top"),sQuery(id+"F0.wireOp",EDGE,"E5"),sQuery(id+"F0.wireOp",EDGE,"E6.MirrorC"),sQuery(id+"F0.wireOp",EDGE,"E7.1.0"),sQuery(id+"F0.wireOp",EDGE,"E7.1.1"),sQuery(id+"F0.wireOp",EDGE,"E7.1.2"),sQuery(id+"F0.wireOp",EDGE,"E7.1.3"),sQuery(id+"F0.wireOp",EDGE,"E7.2.0"),sQuery(id+"F0.wireOp",EDGE,"E7.2.1"),sQuery(id+"F0.wireOp",EDGE,"E7.2.2"),sQuery(id+"F0.wireOp",EDGE,"E7.2.3"),sQuery(id+"F0.wireOp",EDGE,"E7.3.0"),sQuery(id+"F0.wireOp",EDGE,"E7.3.1"),sQuery(id+"F0.wireOp",EDGE,"E7.3.2"),sQuery(id+"F0.wireOp",EDGE,"E7.3.3"),sQuery(id+"F0.wireOp",EDGE,"E83"),sQuery(id+"F0.wireOp",EDGE,"E85.1.1"),sQuery(id+"F0.wireOp",EDGE,"E85.2.1"),sQuery(id+"F0.wireOp",EDGE,"E85.3.1"),sQuery(id+"F0.wireOp",EDGE,"E85.4.1"),sQuery(id+"F0.wireOp",EDGE,"E85.5.1"),sQuery(id+"F0.wireOp",EDGE,"E85.6.1"),sQuery(id+"F0.wireOp",EDGE,"E85.7.1"),sQuery(id+"F0.wireOp",EDGE,"E86"),sQuery(id+"F0.wireOp",EDGE,"E88.2.0"),sQuery(id+"F0.wireOp",EDGE,"E88.3.0"),sQuery(id+"F0.wireOp",EDGE,"E88.4.0"),sQuery(id+"F0.wireOp",EDGE,"E88.6.0"),sQuery(id+"F0.wireOp",EDGE,"E88.8.0"),sQuery(id+"F0.wireOp",EDGE,"E88.9.0"),sQuery(id+"F0.wireOp",EDGE,"E88.10.0"),sQuery(id+"F0.wireOp",EDGE,"E113"),sQuery(id+"F0.wireOp",EDGE,"26b68fcc-744b-4aa5-8645-4a920cf469b9.0.1.1"),sQuery(id+"F0.wireOp",EDGE,"26b68fcc-744b-4aa5-8645-4a920cf469b9.1.0.1"),sQuery(id+"F0.wireOp",EDGE,"26b68fcc-744b-4aa5-8645-4a920cf469b9.1.1.1")])],"isStart":false});
            var sketch = newSketch(context, id + "F4", { "sketchPlane" : qUnion([Q0])});
            skCircle(sketch, "E139", {"center": v(0.02, 57.48) * mm, "radius": 2.75 * mm});
            skCircle(sketch, "E140", {"center": v(0.02, 57.48) * mm, "radius": 4.75 * mm});
            skCircle(sketch, "E141", {"center": v(0.02, 57.48) * mm, "radius": 5.75 * mm});
            skCircle(sketch, "E142", {"center": v(0.02, 57.48) * mm, "radius": 11.75 * mm, "construction": true});
            skLineSegment(sketch, "E143", {"start": v(0, 63.23) * mm, "end": v(0, 69.23) * mm});
            skLineSegment(sketch, "E144.0", {"start": v(-0.75, 63.17) * mm, "end": v(-0.75, 68.48) * mm});
            skCircle(sketch, "E145.0", {"center": v(0.02, 57.48) * mm, "radius": 11 * mm, "construction": true});
            skArc(sketch, "E146", {"start": v(0.75, 68.45) * mm, "mid": v(0.75, 68.46) * mm, "end": v(0.75, 68.48) * mm});
            skLineSegment(sketch, "E147.trimOffspring", {"start": v(-0.75, 69.2) * mm, "end": v(-0.75, 69.23) * mm});
            skLineSegment(sketch, "E148.trimOffspring", {"start": v(0.75, 69.2) * mm, "end": v(0.75, 69.23) * mm});
            skArc(sketch, "E149.trimOffspring", {"start": v(0, 69.23) * mm, "mid": v(-0.54, 69) * mm, "end": v(-0.75, 68.45) * mm});
            skText(sketch, "E150", { "text": "01", "fontName": "OpenSans-Bold.ttf"});
            skText(sketch, "E151", { "text": "03", "fontName": "OpenSans-Bold.ttf"});
            skText(sketch, "E152", { "text": "02", "fontName": "OpenSans-Bold.ttf"});
            skText(sketch, "E153", { "text": "04", "fontName": "OpenSans-Bold.ttf"});
            const initialGuessF4  = {"E150": [-0.0029, 0.03787, 1, 0, 0.004], "E151": [-0.00324, -0.04222, 1, 0, 0.004], "E152": [-0.04353, -0.002, 1, 0, 0.004], "E153": [0.03724, -0.00207, 1, 0, 0.004]};
            skSetInitialGuess(sketch, initialGuessF4);
            skSolve(sketch);
        }
        {
            var Q0;
            Q0=makeQuery(id+"F4.imprint","IMPRINT",FACE,{"disambiguationData":[TD([[makeQuery(id+"F4.imprint","IMPRINT",EDGE,{"derivedFrom":sQuery(id+"F4.wireOp",EDGE,"E140")}),-1.0]])]});
            var Q1;
            Q1=makeQuery(id+"F4.imprint","IMPRINT",FACE,{"disambiguationData":[TD([[makeQuery(id+"F4.imprint","IMPRINT",EDGE,{"derivedFrom":sQuery(id+"F4.wireOp",EDGE,"E139")}),1.0]])]});
            extrude(context, id + "F5", {"entities" : qUnion([Q0, Q1]), "depth" : 2 * mm});
        }
        {
            var Q0;
            {var subQ0=sQuery(id+"F4.wireOp",EDGE,"E143");Q0=makeQuery(id+"F4.imprint","IMPRINT",FACE,{"disambiguationData":[TD([[makeQuery(id+"F4.imprint","IMPRINT",EDGE,{"derivedFrom":subQ0}),1.0]])]});}
            var Q1;
            Q1=sQuery(id+"F4.wireOp",EDGE,"E143");
            revolve(context, id + "F6", {"entities" : qUnion([Q0]), "axis" : qUnion([Q1]), "revolveType" : RevolveType.FULL});
        }
        {
            var Q0;
            Q0=makeQuery(id+"F6.opRevolve","SWEPT_BODY",BODY,{"disambiguationData":[OSD([sQuery(id+"F4.wireOp",EDGE,"E141"),sQuery(id+"F4.wireOp",EDGE,"E143"),sQuery(id+"F4.wireOp",EDGE,"E144.0"),sQuery(id+"F4.wireOp",EDGE,"E149.trimOffspring")])]});
            var Q1;
            Q1=sQuery(id+"F4.wireOp",EDGE,"E140");
            circularPattern(context, id + "F7", {"operationType" : NewBodyOperationType.ADD, "entities" : qUnion([Q0]), "axis" : qUnion([Q1]), "angle" : 22.5 * degree, "instanceCount" : 16});
        }
        {
            var Q0;
            Q0=makeQuery(id+"F5.opExtrude","SWEPT_BODY",BODY,{"disambiguationData":[OSD([sQuery(id+"F0.wireOp",EDGE,"E88.6.0"),sQuery(id+"F4.wireOp",EDGE,"E139")])]});
            var Q1;
            Q1=makeQuery(id+"F5.opExtrude","SWEPT_BODY",BODY,{"disambiguationData":[OSD([sQuery(id+"F4.wireOp",EDGE,"E140"),sQuery(id+"F4.wireOp",EDGE,"E141")])]});
            var Q2;
            Q2=sQuery(id+"F0.wireOp",EDGE,"E18.0");
            circularPattern(context, id + "F8", {"entities" : qUnion([Q0, Q1]), "axis" : qUnion([Q2]), "angle" : 30 * degree, "instanceCount" : 12});
        }
        {
            var Q0;
            Q0=makeQuery(id+"F8.opPattern","COPY",BODY,{"derivedFrom":makeQuery(id+"F5.opExtrude","SWEPT_BODY",BODY,{"disambiguationData":[OSD([sQuery(id+"F4.wireOp",EDGE,"E140"),sQuery(id+"F4.wireOp",EDGE,"E141")])]}),"instanceName":"11"});
            var Q1;
            Q1=makeQuery(id+"F8.opPattern","COPY",BODY,{"derivedFrom":makeQuery(id+"F5.opExtrude","SWEPT_BODY",BODY,{"disambiguationData":[OSD([sQuery(id+"F4.wireOp",EDGE,"E140"),sQuery(id+"F4.wireOp",EDGE,"E141")])]}),"instanceName":"7"});
            var Q2;
            Q2=makeQuery(id+"F8.opPattern","COPY",BODY,{"derivedFrom":makeQuery(id+"F5.opExtrude","SWEPT_BODY",BODY,{"disambiguationData":[OSD([sQuery(id+"F0.wireOp",EDGE,"E88.6.0"),sQuery(id+"F4.wireOp",EDGE,"E139")])]}),"instanceName":"7"});
            var Q3;
            Q3=makeQuery(id+"F8.opPattern","COPY",BODY,{"derivedFrom":makeQuery(id+"F5.opExtrude","SWEPT_BODY",BODY,{"disambiguationData":[OSD([sQuery(id+"F4.wireOp",EDGE,"E140"),sQuery(id+"F4.wireOp",EDGE,"E141")])]}),"instanceName":"5"});
            var Q4;
            Q4=makeQuery(id+"F8.opPattern","COPY",BODY,{"derivedFrom":makeQuery(id+"F5.opExtrude","SWEPT_BODY",BODY,{"disambiguationData":[OSD([sQuery(id+"F0.wireOp",EDGE,"E88.6.0"),sQuery(id+"F4.wireOp",EDGE,"E139")])]}),"instanceName":"5"});
            var Q5;
            Q5=makeQuery(id+"F8.opPattern","COPY",BODY,{"derivedFrom":makeQuery(id+"F5.opExtrude","SWEPT_BODY",BODY,{"disambiguationData":[OSD([sQuery(id+"F0.wireOp",EDGE,"E88.6.0"),sQuery(id+"F4.wireOp",EDGE,"E139")])]}),"instanceName":"1"});
            var Q6;
            Q6=makeQuery(id+"F8.opPattern","COPY",BODY,{"derivedFrom":makeQuery(id+"F5.opExtrude","SWEPT_BODY",BODY,{"disambiguationData":[OSD([sQuery(id+"F4.wireOp",EDGE,"E140"),sQuery(id+"F4.wireOp",EDGE,"E141")])]}),"instanceName":"1"});
            var Q7;
            Q7=makeQuery(id+"F8.opPattern","COPY",BODY,{"derivedFrom":makeQuery(id+"F5.opExtrude","SWEPT_BODY",BODY,{"disambiguationData":[OSD([sQuery(id+"F0.wireOp",EDGE,"E88.6.0"),sQuery(id+"F4.wireOp",EDGE,"E139")])]}),"instanceName":"11"});
            deleteBodies(context, id + "F9", {"entities" : qUnion([Q0, Q1, Q2, Q3, Q4, Q5, Q6, Q7])});
        }
        {
            var Q0;
            Q0=makeQuery(id+"F4.imprint","IMPRINT",FACE,{"disambiguationData":[TD([[makeQuery(id+"F4.imprint","IMPRINT",EDGE,{"derivedFrom":sQuery(id+"F4.wireOp",EDGE,"E152.sketch_text.stroke-0")}),-1.0]])]});
            var Q1;
            Q1=makeQuery(id+"F4.imprint","IMPRINT",FACE,{"disambiguationData":[TD([[makeQuery(id+"F4.imprint","IMPRINT",EDGE,{"derivedFrom":sQuery(id+"F4.wireOp",EDGE,"E152.sketch_text.stroke-16")}),-1.0]])]});
            var Q2;
            Q2=makeQuery(id+"F4.imprint","IMPRINT",FACE,{"disambiguationData":[TD([[makeQuery(id+"F4.imprint","IMPRINT",EDGE,{"derivedFrom":sQuery(id+"F4.wireOp",EDGE,"E150.sketch_text.stroke-0")}),-1.0]])]});
            var Q3;
            Q3=makeQuery(id+"F4.imprint","IMPRINT",FACE,{"disambiguationData":[TD([[makeQuery(id+"F4.imprint","IMPRINT",EDGE,{"derivedFrom":sQuery(id+"F4.wireOp",EDGE,"E150.sketch_text.stroke-16")}),-1.0]])]});
            var Q4;
            Q4=makeQuery(id+"F4.imprint","IMPRINT",FACE,{"disambiguationData":[TD([[makeQuery(id+"F4.imprint","IMPRINT",EDGE,{"derivedFrom":sQuery(id+"F4.wireOp",EDGE,"E153.sketch_text.stroke-0")}),-1.0]])]});
            var Q5;
            Q5=makeQuery(id+"F4.imprint","IMPRINT",FACE,{"disambiguationData":[TD([[makeQuery(id+"F4.imprint","IMPRINT",EDGE,{"derivedFrom":sQuery(id+"F4.wireOp",EDGE,"E153.sketch_text.stroke-16")}),-1.0]])]});
            var Q6;
            Q6=makeQuery(id+"F4.imprint","IMPRINT",FACE,{"disambiguationData":[TD([[makeQuery(id+"F4.imprint","IMPRINT",EDGE,{"derivedFrom":sQuery(id+"F4.wireOp",EDGE,"E151.sketch_text.stroke-0")}),-1.0]])]});
            var Q7;
            Q7=makeQuery(id+"F4.imprint","IMPRINT",FACE,{"disambiguationData":[TD([[makeQuery(id+"F4.imprint","IMPRINT",EDGE,{"derivedFrom":sQuery(id+"F4.wireOp",EDGE,"E151.sketch_text.stroke-16")}),-1.0]])]});
            extrude(context, id + "F10", {"entities" : qUnion([Q0, Q1, Q2, Q3, Q4, Q5, Q6, Q7]), "operationType" : NewBodyOperationType.ADD, "depth" : 1 * mm});
        }
        {
            var Q0;
            Q0=makeQuery(id+"F0.imprint","IMPRINT",FACE,{"disambiguationData":[TD([[makeQuery(id+"F0.imprint","IMPRINT",EDGE,{"derivedFrom":sQuery(id+"F0.wireOp",EDGE,"E119.sketch_text.stroke-0")}),-1.0]])]});
            extrude(context, id + "F11", {"entities" : qUnion([Q0]), "depth" : .5 * mm});
        }
        {
            var Q0;
            Q0=makeQuery(id+"F11.opExtrude","SWEPT_BODY",BODY,{"disambiguationData":[OSD([sQuery(id+"F0.wireOp",EDGE,"E119.sketch_text.stroke-0"),sQuery(id+"F0.wireOp",EDGE,"E119.sketch_text.stroke-1"),sQuery(id+"F0.wireOp",EDGE,"E119.sketch_text.stroke-2"),sQuery(id+"F0.wireOp",EDGE,"E119.sketch_text.stroke-3"),sQuery(id+"F0.wireOp",EDGE,"E119.sketch_text.stroke-4"),sQuery(id+"F0.wireOp",EDGE,"E119.sketch_text.stroke-5"),sQuery(id+"F0.wireOp",EDGE,"E119.sketch_text.stroke-6"),sQuery(id+"F0.wireOp",EDGE,"E119.sketch_text.stroke-7"),sQuery(id+"F0.wireOp",EDGE,"E119.sketch_text.stroke-8"),sQuery(id+"F0.wireOp",EDGE,"E119.sketch_text.stroke-9"),sQuery(id+"F0.wireOp",EDGE,"E119.sketch_text.stroke-10"),sQuery(id+"F0.wireOp",EDGE,"E119.sketch_text.stroke-11")])]});
            var Q1;
            Q1=sQuery(id+"F0.wireOp",EDGE,"E1");
            circularPattern(context, id + "F12", {"operationType" : NewBodyOperationType.ADD, "entities" : qUnion([Q0]), "axis" : qUnion([Q1]), "angle" : 60 * degree, "instanceCount" : 6});
        }
    });
